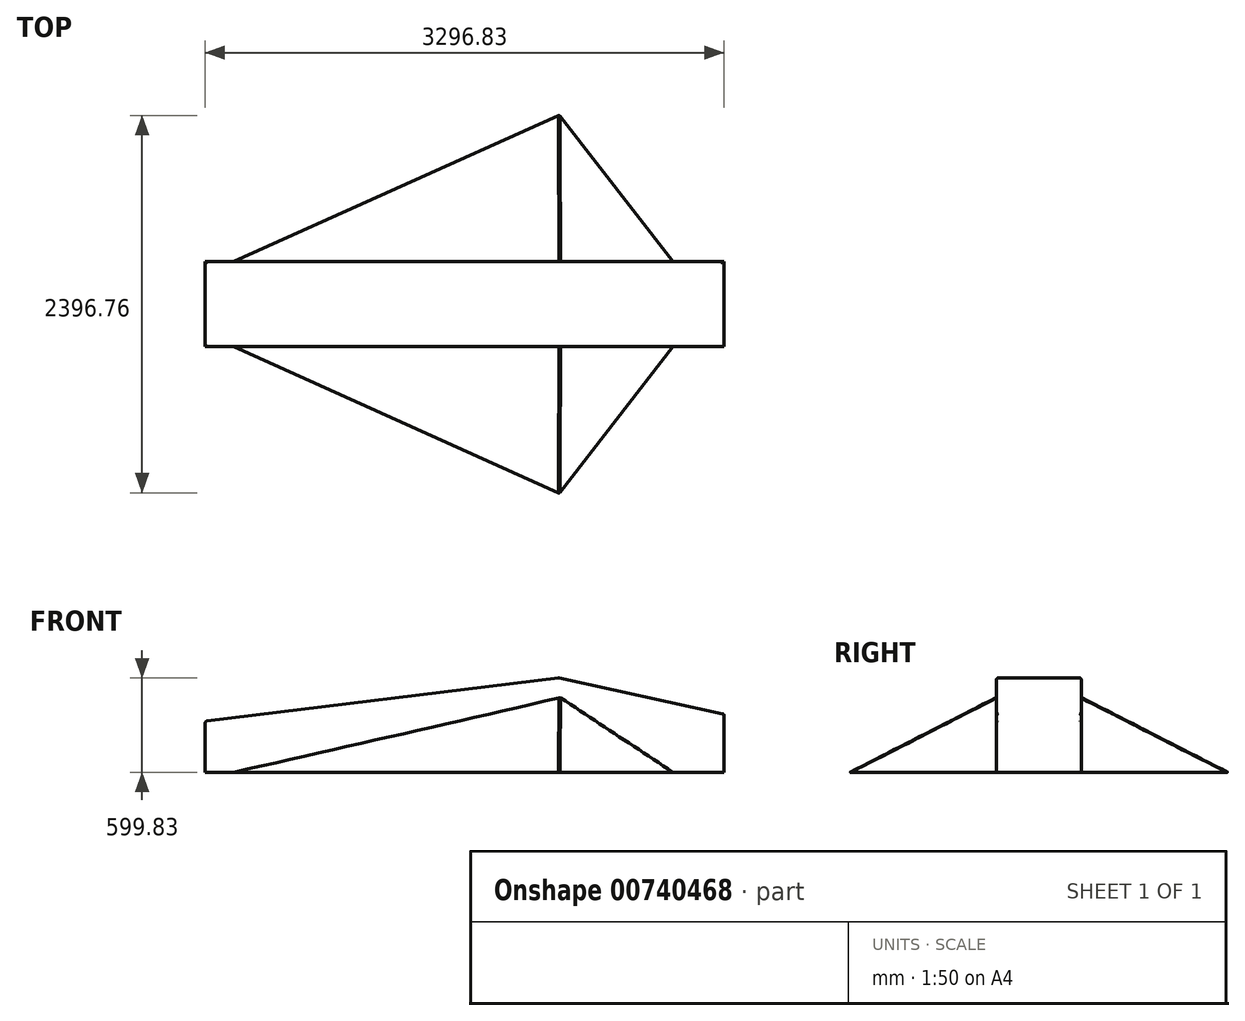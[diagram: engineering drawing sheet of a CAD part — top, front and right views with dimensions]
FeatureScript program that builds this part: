
annotation { "Feature Type Name" : "Feature", "Feature Type Description" : "" }
export const myFeature = defineFeature(function(context is Context, id is Id, definition is map)
    precondition{}
    {
        {
            var Q0;
            Q0=qCreatedBy(makeId("Top.planeOp"),FACE);
            var sketch = newSketch(context, id + "F0", { "sketchPlane" : qUnion([Q0])});
            skLineSegment(sketch, "E0.bottom", {"start": v(1800, 1200) * mm, "end": v(-1800, 1200) * mm});
            skLineSegment(sketch, "E0.top", {"start": v(1800, -1200) * mm, "end": v(-1800, -1200) * mm});
            skLineSegment(sketch, "E0.left", {"start": v(1800, 1200) * mm, "end": v(1800, -1200) * mm});
            skLineSegment(sketch, "E0.right", {"start": v(-1800, 1200) * mm, "end": v(-1800, -1200) * mm});
            skPoint(sketch, "E0.middle", {"position": v(0, 0) * mm});
            skLineSegment(sketch, "E1", {"start": v(-1800, 0) * mm, "end": v(868.06, 1200) * mm});
            skLineSegment(sketch, "E2", {"start": v(868.06, 1200) * mm, "end": v(1800, 0) * mm});
            skLineSegment(sketch, "E3", {"start": v(1800, 0) * mm, "end": v(868.06, -1200) * mm});
            skLineSegment(sketch, "E4", {"start": v(868.06, -1200) * mm, "end": v(-1800, 0) * mm});
            skPoint(sketch, "E5", {"position": v(868.06, 0) * mm});
            skSolve(sketch);
        }
        {
            var Q0;
            Q0=makeQuery(id+"F0.imprint","IMPRINT",FACE,{"disambiguationData":[TD([[makeQuery(id+"F0.imprint","IMPRINT",EDGE,{"derivedFrom":sQuery(id+"F0.wireOp",EDGE,"E1")}),-1.0]])]});
            cPlane(context, id + "F1", {"entities" : qUnion([Q0]), "cplaneType" : CPlaneType.OFFSET, "offset" : 600 * mm, "width" : 150 * mm, "height" : 150 * mm});
        }
        {
            var Q0;
            Q0=qCreatedBy(id+"F1.planeOp",FACE);
            var sketch = newSketch(context, id + "F2", { "sketchPlane" : qUnion([Q0])});
            skPoint(sketch, "E6.middle", {"position": v(874, 0) * mm});
            skLineSegment(sketch, "E7", {"start": v(874, 25) * mm, "end": v(849, 0) * mm});
            skLineSegment(sketch, "E8", {"start": v(849, 0) * mm, "end": v(874, -25) * mm});
            skLineSegment(sketch, "E9", {"start": v(874, -25) * mm, "end": v(899, 0) * mm});
            skLineSegment(sketch, "E10", {"start": v(899, 0) * mm, "end": v(874, 25) * mm});
            skPoint(sketch, "E11.orphan", {"position": v(849, 25) * mm});
            skPoint(sketch, "E6.right.end.orphan", {"position": v(849, -25) * mm});
            skPoint(sketch, "E12.orphan", {"position": v(899, -25) * mm});
            skPoint(sketch, "E6.bottom.start.orphan", {"position": v(899, 25) * mm});
            skSolve(sketch);
        }
        {
            var Q0;
            Q0=makeQuery(id+"F0.imprint","IMPRINT",FACE,{"disambiguationData":[TD([[makeQuery(id+"F0.imprint","IMPRINT",EDGE,{"derivedFrom":sQuery(id+"F0.wireOp",EDGE,"E1")}),-1.0]])]});
            var Q1;
            Q1=makeQuery(id+"F2.imprint","IMPRINT",FACE,{"disambiguationData":[TD([[makeQuery(id+"F2.imprint","IMPRINT",EDGE,{"derivedFrom":sQuery(id+"F2.wireOp",EDGE,"E7")}),1.0]])]});
            loft(context, id + "F3", {"sheetProfilesArray" : [{ "sheetProfileEntities" : qUnion([Q0]) }, { "sheetProfileEntities" : qUnion([Q1]) }]});
        }
        {
            var Q0;
            Q0=makeQuery(id+"F0.imprint","IMPRINT",FACE,{"disambiguationData":[TD([[makeQuery(id+"F0.imprint","IMPRINT",EDGE,{"derivedFrom":sQuery(id+"F0.wireOp",EDGE,"E1")}),-1.0]])]});
            var sketch = newSketch(context, id + "F4", { "sketchPlane" : qUnion([Q0])});
            skLineSegment(sketch, "E13.bottom", {"start": v(1916.43, -269.62) * mm, "end": v(-1916.43, -269.62) * mm});
            skLineSegment(sketch, "E13.top", {"start": v(1916.43, 269.62) * mm, "end": v(-1916.43, 269.62) * mm});
            skLineSegment(sketch, "E13.left", {"start": v(1916.43, -269.62) * mm, "end": v(1916.43, 269.62) * mm});
            skLineSegment(sketch, "E13.right", {"start": v(-1916.43, -269.62) * mm, "end": v(-1916.43, 269.62) * mm});
            skPoint(sketch, "E13.middle", {"position": v(0, 0) * mm});
            skSolve(sketch);
        }
        {
            var Q0;
            {var subQ7=sQuery(id+"F4.wireOp",EDGE,"E13.bottom");var subQ9=makeQuery(id+"F0.imprint","IMPRINT",EDGE,{"derivedFrom":sQuery(id+"F0.wireOp",EDGE,"E3")});var subQ11=makeQuery(id+"F4.imprint","INTERSECT",VERTEX,{"derivedFrom":[subQ9,subQ7]});Q0=makeQuery(id+"F4.imprint","IMPRINT",FACE,{"disambiguationData":[TD([[makeQuery(id+"F4.imprint","IMPRINT",EDGE,{"disambiguationData":[TD([[subQ11,-1.0]])],"derivedFrom":subQ7}),-1.0]])]});}
            var Q1;
            {var subQ5=sQuery(id+"F4.wireOp",EDGE,"E13.right");Q1=makeQuery(id+"F4.imprint","IMPRINT",FACE,{"disambiguationData":[TD([[makeQuery(id+"F4.imprint","IMPRINT",EDGE,{"derivedFrom":subQ5}),-1.0]])]});}
            var Q2;
            {var subQ5=sQuery(id+"F4.wireOp",EDGE,"E13.left");Q2=makeQuery(id+"F4.imprint","IMPRINT",FACE,{"disambiguationData":[TD([[makeQuery(id+"F4.imprint","IMPRINT",EDGE,{"derivedFrom":subQ5}),1.0]])]});}
            extrude(context, id + "F5", {"entities" : qUnion([Q0, Q1, Q2]), "operationType" : NewBodyOperationType.ADD, "depth" : 600 * mm, "offsetDistance" : 25 * mm});
        }
        {
            var Q0;
            Q0=makeQuery(id+"F5.opExtrude","SWEPT_FACE",FACE,{"disambiguationData":[OSD([sQuery(id+"F4.wireOp",EDGE,"E13.bottom")])]});
            var sketch = newSketch(context, id + "F6", { "sketchPlane" : qUnion([Q0])});
            skLineSegment(sketch, "E14", {"start": v(865.41, 600) * mm, "end": v(-1380.4, 323.73) * mm});
            skLineSegment(sketch, "E15", {"start": v(-1380.4, 323.73) * mm, "end": v(-1380.4, 0) * mm});
            skLineSegment(sketch, "E16", {"start": v(865.41, 600) * mm, "end": v(1916.43, 370.36) * mm});
            skSolve(sketch);
        }
        {
            var Q0;
            {var subQ5=sQuery(id+"F6.wireOp",EDGE,"E14");Q0=makeQuery(id+"F6.imprint","IMPRINT",FACE,{"disambiguationData":[TD([[makeQuery(id+"F6.imprint","IMPRINT",EDGE,{"derivedFrom":subQ5}),-1.0]])]});}
            var Q1;
            {var subQ0=sQuery(id+"F6.wireOp",EDGE,"E16");Q1=makeQuery(id+"F6.imprint","IMPRINT",FACE,{"disambiguationData":[TD([[makeQuery(id+"F6.imprint","IMPRINT",EDGE,{"derivedFrom":subQ0}),1.0]])]});}
            extrude(context, id + "F7", {"entities" : qUnion([Q0, Q1]), "operationType" : NewBodyOperationType.REMOVE, "endBound" : BoundingType.THROUGH_ALL, "oppositeDirection" : true, "depth" : 25 * mm, "offsetDistance" : 25 * mm});
        }
        {
            var Q0;
            Q0=makeQuery(id+"F3.opLoft","SWEPT_EDGE",EDGE,{"disambiguationData":[OSD([sQuery(id+"F0.wireOp",EDGE,"E0.top"),sQuery(id+"F0.wireOp",EDGE,"E3"),sQuery(id+"F0.wireOp",EDGE,"E4"),sQuery(id+"F2.wireOp",EDGE,"E8"),sQuery(id+"F2.wireOp",EDGE,"E9")])]});
            var Q1;
            Q1=makeQuery(id+"F7.boolean.opBoolean","COPY",EDGE,{"derivedFrom":makeQuery(id+"F7.opExtrude","CAP_EDGE",EDGE,{"disambiguationData":[OSD([sQuery(id+"F6.wireOp",EDGE,"E16")])],"isStart":true})});
            var Q2;
            Q2=makeQuery(id+"F7.boolean.opBoolean","COPY",EDGE,{"derivedFrom":makeQuery(id+"F7.opExtrude","SWEPT_EDGE",EDGE,{"disambiguationData":[OSD([sQuery(id+"F4.wireOp",EDGE,"E13.bottom"),sQuery(id+"F4.wireOp",EDGE,"E13.left"),sQuery(id+"F6.wireOp",EDGE,"E16")])]})});
            var Q3;
            {var subQ0=sQuery(id+"F6.wireOp",EDGE,"E16");var subQ1=sQuery(id+"F6.wireOp",EDGE,"E14");var subQ2=sQuery(id+"F4.wireOp",EDGE,"E13.bottom");Q3=makeQuery(id+"F7.boolean.opBoolean","TWEAK_EDGE",EDGE,{"derivedFrom":[makeQuery(id+"F7.opExtrude","SWEPT_EDGE",EDGE,{"disambiguationData":[OSD([subQ2,subQ1,subQ0]),OD(0.0)]}),makeQuery(id+"F7.opExtrude","SWEPT_EDGE",EDGE,{"disambiguationData":[OSD([subQ2,subQ1,subQ0]),OD(1.0)]})]});}
            var Q4;
            Q4=makeQuery(id+"F7.boolean.opBoolean","COPY",EDGE,{"derivedFrom":makeQuery(id+"F7.opExtrude","CAP_EDGE",EDGE,{"disambiguationData":[OSD([sQuery(id+"F6.wireOp",EDGE,"E14")])],"isStart":true})});
            var Q5;
            Q5=makeQuery(id+"F7.boolean.opBoolean","COPY",FACE,{"derivedFrom":makeQuery(id+"F7.opExtrude","SWEPT_FACE",FACE,{"disambiguationData":[OSD([sQuery(id+"F6.wireOp",EDGE,"E14")])]})});
            var Q6;
            Q6=makeQuery(id+"F7.boolean.opBoolean","COPY",FACE,{"derivedFrom":makeQuery(id+"F7.opExtrude","SWEPT_FACE",FACE,{"disambiguationData":[OSD([sQuery(id+"F6.wireOp",EDGE,"E16")])]})});
            var Q7;
            Q7=makeQuery(id+"F3.opLoft","SWEPT_EDGE",EDGE,{"disambiguationData":[OSD([sQuery(id+"F0.wireOp",EDGE,"E0.bottom"),sQuery(id+"F0.wireOp",EDGE,"E1"),sQuery(id+"F0.wireOp",EDGE,"E2"),sQuery(id+"F2.wireOp",EDGE,"E7"),sQuery(id+"F2.wireOp",EDGE,"E10")])]});
            fillet(context, id + "F8", {"entities" : qUnion([Q0, Q1, Q2, Q3, Q4, Q5, Q6, Q7]), "radius" : 13 * mm, "tangentPropagation" : true, "allowEdgeOverflow" : false});
        }
    });
